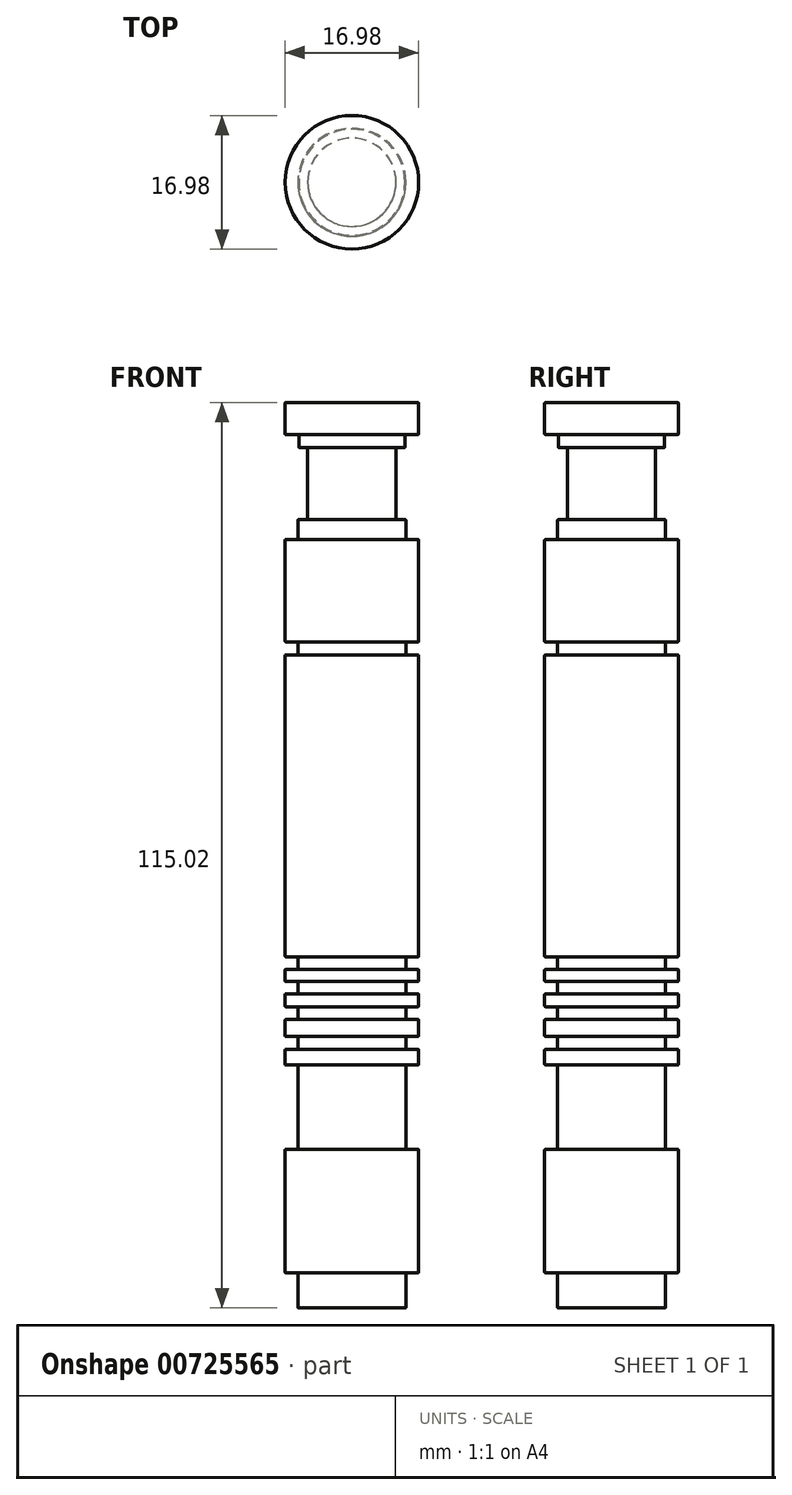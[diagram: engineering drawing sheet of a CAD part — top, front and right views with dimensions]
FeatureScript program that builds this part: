
annotation { "Feature Type Name" : "Feature", "Feature Type Description" : "" }
export const myFeature = defineFeature(function(context is Context, id is Id, definition is map)
    precondition{}
    {
        {
            var Q0;
            Q0=qCreatedBy(makeId("Right.planeOp"),FACE);
            var sketch = newSketch(context, id + "F0", { "sketchPlane" : qUnion([Q0])});
            skLineSegment(sketch, "E0", {"start": v(0, 0) * mm, "end": v(-6.85, 0) * mm});
            skLineSegment(sketch, "E1", {"start": v(-6.85, 0) * mm, "end": v(-6.85, 4.49) * mm});
            skLineSegment(sketch, "E2", {"start": v(-6.85, 4.49) * mm, "end": v(-8.49, 4.49) * mm});
            skLineSegment(sketch, "E3", {"start": v(-8.49, 4.49) * mm, "end": v(-8.49, 20.16) * mm});
            skLineSegment(sketch, "E4", {"start": v(-8.49, 20.16) * mm, "end": v(-6.85, 20.16) * mm});
            skLineSegment(sketch, "E5", {"start": v(-6.85, 20.16) * mm, "end": v(-6.85, 30.88) * mm});
            skLineSegment(sketch, "E6", {"start": v(-6.85, 30.88) * mm, "end": v(-8.49, 30.88) * mm});
            skLineSegment(sketch, "E7", {"start": v(-8.49, 30.88) * mm, "end": v(-8.49, 32.86) * mm});
            skLineSegment(sketch, "E8", {"start": v(-8.49, 32.86) * mm, "end": v(-6.85, 32.86) * mm});
            skLineSegment(sketch, "E9", {"start": v(-6.85, 32.86) * mm, "end": v(-6.85, 34.51) * mm});
            skLineSegment(sketch, "E10", {"start": v(-6.85, 34.51) * mm, "end": v(-8.49, 34.51) * mm});
            skLineSegment(sketch, "E11", {"start": v(-8.49, 34.51) * mm, "end": v(-8.49, 36.65) * mm});
            skLineSegment(sketch, "E12", {"start": v(-8.49, 36.65) * mm, "end": v(-6.85, 36.65) * mm});
            skLineSegment(sketch, "E13", {"start": v(-6.85, 36.65) * mm, "end": v(-6.85, 38.29) * mm});
            skLineSegment(sketch, "E14", {"start": v(-6.85, 38.29) * mm, "end": v(-8.49, 38.29) * mm});
            skLineSegment(sketch, "E15", {"start": v(-8.49, 38.29) * mm, "end": v(-8.49, 39.9) * mm});
            skLineSegment(sketch, "E16", {"start": v(-8.49, 39.9) * mm, "end": v(-6.85, 39.9) * mm});
            skLineSegment(sketch, "E17", {"start": v(-6.85, 39.9) * mm, "end": v(-6.85, 41.48) * mm});
            skLineSegment(sketch, "E18", {"start": v(-6.85, 41.48) * mm, "end": v(-8.49, 41.48) * mm});
            skLineSegment(sketch, "E19", {"start": v(-8.49, 41.48) * mm, "end": v(-8.49, 43) * mm});
            skLineSegment(sketch, "E20", {"start": v(-8.49, 43) * mm, "end": v(-6.85, 43) * mm});
            skLineSegment(sketch, "E21", {"start": v(-6.85, 43) * mm, "end": v(-6.85, 44.63) * mm});
            skLineSegment(sketch, "E22", {"start": v(-6.85, 44.63) * mm, "end": v(-8.49, 44.63) * mm});
            skLineSegment(sketch, "E23", {"start": v(-8.49, 44.63) * mm, "end": v(-8.49, 82.98) * mm});
            skLineSegment(sketch, "E24", {"start": v(-8.49, 82.98) * mm, "end": v(-6.85, 82.98) * mm});
            skLineSegment(sketch, "E25", {"start": v(-6.85, 82.98) * mm, "end": v(-6.85, 84.63) * mm});
            skLineSegment(sketch, "E26", {"start": v(-6.85, 84.63) * mm, "end": v(-8.49, 84.63) * mm});
            skLineSegment(sketch, "E27", {"start": v(-8.49, 84.63) * mm, "end": v(-8.49, 97.62) * mm});
            skLineSegment(sketch, "E28", {"start": v(-8.49, 97.62) * mm, "end": v(-6.85, 97.62) * mm});
            skLineSegment(sketch, "E29", {"start": v(-6.85, 97.62) * mm, "end": v(-6.85, 100.16) * mm});
            skLineSegment(sketch, "E30", {"start": v(-6.85, 100.16) * mm, "end": v(-5.61, 100.16) * mm});
            skLineSegment(sketch, "E31", {"start": v(-5.61, 100.16) * mm, "end": v(-5.61, 109.3) * mm});
            skLineSegment(sketch, "E32", {"start": v(-5.61, 109.3) * mm, "end": v(-6.75, 109.3) * mm});
            skLineSegment(sketch, "E33", {"start": v(-6.75, 109.3) * mm, "end": v(-6.75, 110.97) * mm});
            skLineSegment(sketch, "E34", {"start": v(-6.75, 110.97) * mm, "end": v(-8.49, 110.97) * mm});
            skLineSegment(sketch, "E35", {"start": v(-8.49, 110.97) * mm, "end": v(-8.49, 115.02) * mm});
            skLineSegment(sketch, "E36", {"start": v(-8.49, 115.02) * mm, "end": v(0, 115.02) * mm});
            skLineSegment(sketch, "E37", {"start": v(0, 115.02) * mm, "end": v(0, 0) * mm});
            skSolve(sketch);
        }
        {
            var Q0;
            Q0=makeQuery(id+"F0.imprint","IMPRINT",FACE,{"disambiguationData":[TD([[makeQuery(id+"F0.imprint","IMPRINT",EDGE,{"derivedFrom":sQuery(id+"F0.wireOp",EDGE,"E0")}),-1.0]])]});
            var Q1;
            Q1=sQuery(id+"F0.wireOp",EDGE,"E37");
            revolve(context, id + "F1", {"surfaceOperationType" : NewSurfaceOperationType.NEW, "entities" : qUnion([Q0]), "axis" : qUnion([Q1]), "revolveType" : RevolveType.FULL});
        }
        {
            var Q0;
            Q0=makeQuery(id+"F1.opRevolve","SWEPT_EDGE",EDGE,{"disambiguationData":[OSD([sQuery(id+"F0.wireOp",EDGE,"E35"),sQuery(id+"F0.wireOp",EDGE,"E36")])]});
            var Q1;
            Q1=makeQuery(id+"F1.opRevolve","SWEPT_EDGE",EDGE,{"disambiguationData":[OSD([sQuery(id+"F0.wireOp",EDGE,"E34"),sQuery(id+"F0.wireOp",EDGE,"E35")])]});
            var Q2;
            Q2=makeQuery(id+"F1.opRevolve","SWEPT_EDGE",EDGE,{"disambiguationData":[OSD([sQuery(id+"F0.wireOp",EDGE,"E33"),sQuery(id+"F0.wireOp",EDGE,"E34")])]});
            var Q3;
            Q3=makeQuery(id+"F1.opRevolve","SWEPT_EDGE",EDGE,{"disambiguationData":[OSD([sQuery(id+"F0.wireOp",EDGE,"E32"),sQuery(id+"F0.wireOp",EDGE,"E33")])]});
            var Q4;
            Q4=makeQuery(id+"F1.opRevolve","SWEPT_EDGE",EDGE,{"disambiguationData":[OSD([sQuery(id+"F0.wireOp",EDGE,"E31"),sQuery(id+"F0.wireOp",EDGE,"E32")])]});
            var Q5;
            Q5=makeQuery(id+"F1.opRevolve","SWEPT_EDGE",EDGE,{"disambiguationData":[OSD([sQuery(id+"F0.wireOp",EDGE,"E29"),sQuery(id+"F0.wireOp",EDGE,"E30")])]});
            var Q6;
            Q6=makeQuery(id+"F1.opRevolve","SWEPT_EDGE",EDGE,{"disambiguationData":[OSD([sQuery(id+"F0.wireOp",EDGE,"E27"),sQuery(id+"F0.wireOp",EDGE,"E28")])]});
            var Q7;
            Q7=makeQuery(id+"F1.opRevolve","SWEPT_EDGE",EDGE,{"disambiguationData":[OSD([sQuery(id+"F0.wireOp",EDGE,"E30"),sQuery(id+"F0.wireOp",EDGE,"E31")])]});
            var Q8;
            Q8=makeQuery(id+"F1.opRevolve","SWEPT_EDGE",EDGE,{"disambiguationData":[OSD([sQuery(id+"F0.wireOp",EDGE,"E28"),sQuery(id+"F0.wireOp",EDGE,"E29")])]});
            var Q9;
            Q9=makeQuery(id+"F1.opRevolve","SWEPT_EDGE",EDGE,{"disambiguationData":[OSD([sQuery(id+"F0.wireOp",EDGE,"E26"),sQuery(id+"F0.wireOp",EDGE,"E27")])]});
            var Q10;
            Q10=makeQuery(id+"F1.opRevolve","SWEPT_EDGE",EDGE,{"disambiguationData":[OSD([sQuery(id+"F0.wireOp",EDGE,"E24"),sQuery(id+"F0.wireOp",EDGE,"E25")])]});
            var Q11;
            Q11=makeQuery(id+"F1.opRevolve","SWEPT_EDGE",EDGE,{"disambiguationData":[OSD([sQuery(id+"F0.wireOp",EDGE,"E23"),sQuery(id+"F0.wireOp",EDGE,"E24")])]});
            var Q12;
            Q12=makeQuery(id+"F1.opRevolve","SWEPT_EDGE",EDGE,{"disambiguationData":[OSD([sQuery(id+"F0.wireOp",EDGE,"E25"),sQuery(id+"F0.wireOp",EDGE,"E26")])]});
            var Q13;
            Q13=makeQuery(id+"F1.opRevolve","SWEPT_EDGE",EDGE,{"disambiguationData":[OSD([sQuery(id+"F0.wireOp",EDGE,"E22"),sQuery(id+"F0.wireOp",EDGE,"E23")])]});
            var Q14;
            Q14=makeQuery(id+"F1.opRevolve","SWEPT_EDGE",EDGE,{"disambiguationData":[OSD([sQuery(id+"F0.wireOp",EDGE,"E19"),sQuery(id+"F0.wireOp",EDGE,"E20")])]});
            var Q15;
            Q15=makeQuery(id+"F1.opRevolve","SWEPT_EDGE",EDGE,{"disambiguationData":[OSD([sQuery(id+"F0.wireOp",EDGE,"E18"),sQuery(id+"F0.wireOp",EDGE,"E19")])]});
            var Q16;
            Q16=makeQuery(id+"F1.opRevolve","SWEPT_EDGE",EDGE,{"disambiguationData":[OSD([sQuery(id+"F0.wireOp",EDGE,"E15"),sQuery(id+"F0.wireOp",EDGE,"E16")])]});
            var Q17;
            Q17=makeQuery(id+"F1.opRevolve","SWEPT_EDGE",EDGE,{"disambiguationData":[OSD([sQuery(id+"F0.wireOp",EDGE,"E14"),sQuery(id+"F0.wireOp",EDGE,"E15")])]});
            var Q18;
            Q18=makeQuery(id+"F1.opRevolve","SWEPT_EDGE",EDGE,{"disambiguationData":[OSD([sQuery(id+"F0.wireOp",EDGE,"E11"),sQuery(id+"F0.wireOp",EDGE,"E12")])]});
            var Q19;
            Q19=makeQuery(id+"F1.opRevolve","SWEPT_EDGE",EDGE,{"disambiguationData":[OSD([sQuery(id+"F0.wireOp",EDGE,"E10"),sQuery(id+"F0.wireOp",EDGE,"E11")])]});
            var Q20;
            Q20=makeQuery(id+"F1.opRevolve","SWEPT_EDGE",EDGE,{"disambiguationData":[OSD([sQuery(id+"F0.wireOp",EDGE,"E7"),sQuery(id+"F0.wireOp",EDGE,"E8")])]});
            var Q21;
            Q21=makeQuery(id+"F1.opRevolve","SWEPT_EDGE",EDGE,{"disambiguationData":[OSD([sQuery(id+"F0.wireOp",EDGE,"E6"),sQuery(id+"F0.wireOp",EDGE,"E7")])]});
            var Q22;
            Q22=makeQuery(id+"F1.opRevolve","SWEPT_EDGE",EDGE,{"disambiguationData":[OSD([sQuery(id+"F0.wireOp",EDGE,"E4"),sQuery(id+"F0.wireOp",EDGE,"E5")])]});
            var Q23;
            Q23=makeQuery(id+"F1.opRevolve","SWEPT_EDGE",EDGE,{"disambiguationData":[OSD([sQuery(id+"F0.wireOp",EDGE,"E3"),sQuery(id+"F0.wireOp",EDGE,"E4")])]});
            var Q24;
            Q24=makeQuery(id+"F1.opRevolve","SWEPT_EDGE",EDGE,{"disambiguationData":[OSD([sQuery(id+"F0.wireOp",EDGE,"E2"),sQuery(id+"F0.wireOp",EDGE,"E3")])]});
            var Q25;
            Q25=makeQuery(id+"F1.opRevolve","SWEPT_EDGE",EDGE,{"disambiguationData":[OSD([sQuery(id+"F0.wireOp",EDGE,"E0"),sQuery(id+"F0.wireOp",EDGE,"E1")])]});
            var Q26;
            Q26=makeQuery(id+"F1.opRevolve","SWEPT_EDGE",EDGE,{"disambiguationData":[OSD([sQuery(id+"F0.wireOp",EDGE,"E1"),sQuery(id+"F0.wireOp",EDGE,"E2")])]});
            var Q27;
            Q27=makeQuery(id+"F1.opRevolve","SWEPT_EDGE",EDGE,{"disambiguationData":[OSD([sQuery(id+"F0.wireOp",EDGE,"E5"),sQuery(id+"F0.wireOp",EDGE,"E6")])]});
            var Q28;
            Q28=makeQuery(id+"F1.opRevolve","SWEPT_EDGE",EDGE,{"disambiguationData":[OSD([sQuery(id+"F0.wireOp",EDGE,"E9"),sQuery(id+"F0.wireOp",EDGE,"E10")])]});
            var Q29;
            Q29=makeQuery(id+"F1.opRevolve","SWEPT_EDGE",EDGE,{"disambiguationData":[OSD([sQuery(id+"F0.wireOp",EDGE,"E13"),sQuery(id+"F0.wireOp",EDGE,"E14")])]});
            var Q30;
            Q30=makeQuery(id+"F1.opRevolve","SWEPT_EDGE",EDGE,{"disambiguationData":[OSD([sQuery(id+"F0.wireOp",EDGE,"E17"),sQuery(id+"F0.wireOp",EDGE,"E18")])]});
            var Q31;
            Q31=makeQuery(id+"F1.opRevolve","SWEPT_EDGE",EDGE,{"disambiguationData":[OSD([sQuery(id+"F0.wireOp",EDGE,"E21"),sQuery(id+"F0.wireOp",EDGE,"E22")])]});
            var Q32;
            Q32=makeQuery(id+"F1.opRevolve","SWEPT_EDGE",EDGE,{"disambiguationData":[OSD([sQuery(id+"F0.wireOp",EDGE,"E8"),sQuery(id+"F0.wireOp",EDGE,"E9")])]});
            var Q33;
            Q33=makeQuery(id+"F1.opRevolve","SWEPT_EDGE",EDGE,{"disambiguationData":[OSD([sQuery(id+"F0.wireOp",EDGE,"E12"),sQuery(id+"F0.wireOp",EDGE,"E13")])]});
            var Q34;
            Q34=makeQuery(id+"F1.opRevolve","SWEPT_EDGE",EDGE,{"disambiguationData":[OSD([sQuery(id+"F0.wireOp",EDGE,"E16"),sQuery(id+"F0.wireOp",EDGE,"E17")])]});
            var Q35;
            Q35=makeQuery(id+"F1.opRevolve","SWEPT_EDGE",EDGE,{"disambiguationData":[OSD([sQuery(id+"F0.wireOp",EDGE,"E20"),sQuery(id+"F0.wireOp",EDGE,"E21")])]});
            fillet(context, id + "F2", {"entities" : qUnion([Q0, Q1, Q2, Q3, Q4, Q5, Q6, Q7, Q8, Q9, Q10, Q11, Q12, Q13, Q14, Q15, Q16, Q17, Q18, Q19, Q20, Q21, Q22, Q23, Q24, Q25, Q26, Q27, Q28, Q29, Q30, Q31, Q32, Q33, Q34, Q35]), "radius" : 0.08 * mm, "tangentPropagation" : true, "allowEdgeOverflow" : false});
        }
    });
